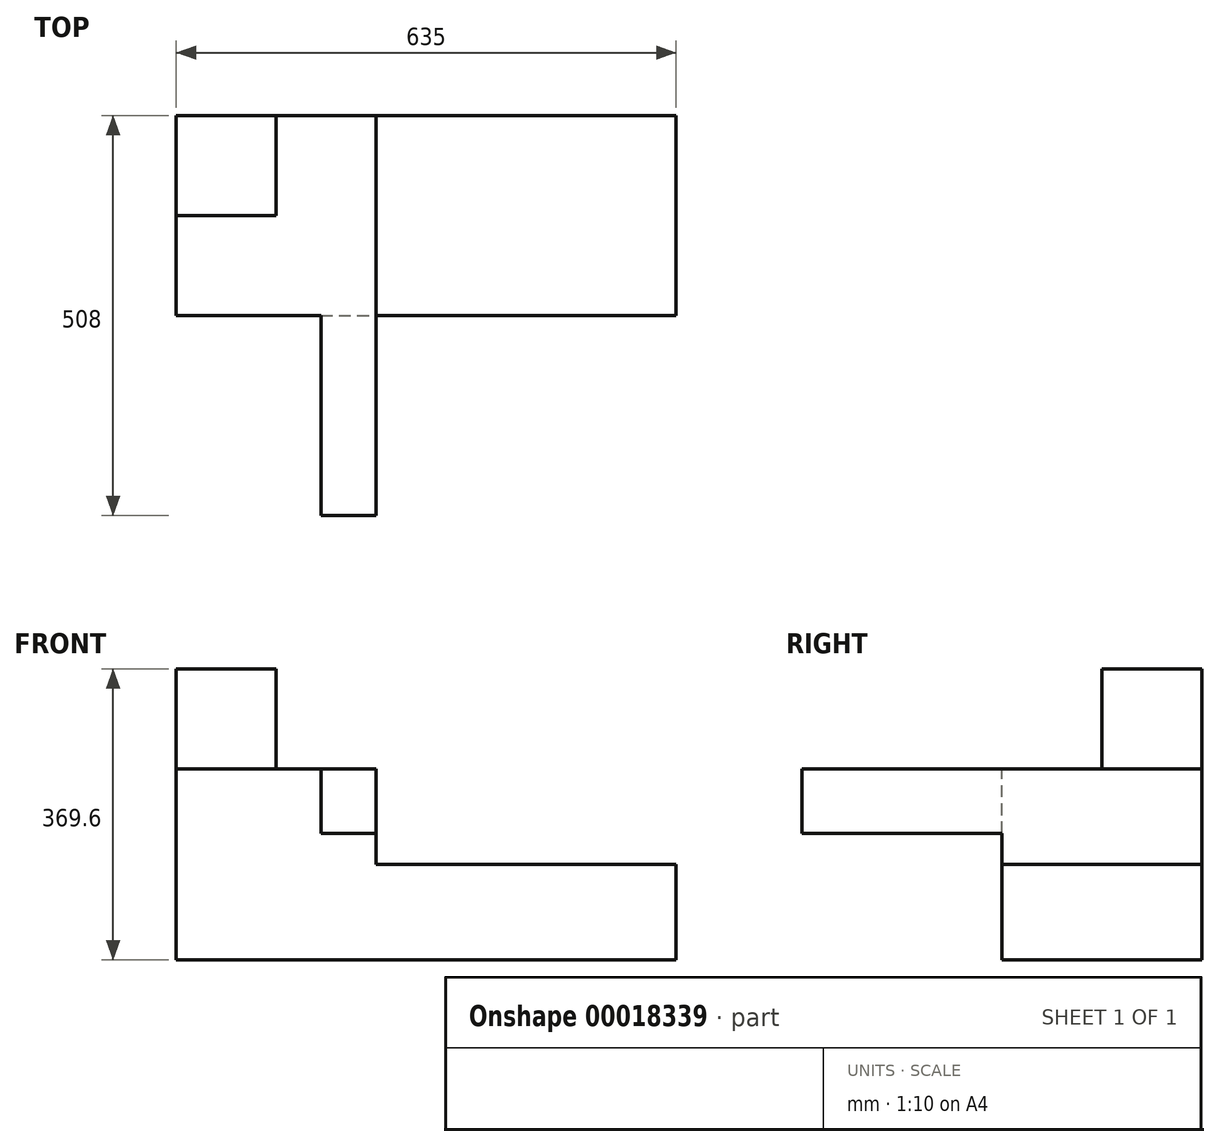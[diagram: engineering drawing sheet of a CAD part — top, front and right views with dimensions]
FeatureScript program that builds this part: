
annotation { "Feature Type Name" : "Feature", "Feature Type Description" : "" }
export const myFeature = defineFeature(function(context is Context, id is Id, definition is map)
    precondition{}
    {
        {
            var Q0;
            Q0=qCreatedBy(makeId("Front.planeOp"),FACE);
            var sketch = newSketch(context, id + "F0", { "sketchPlane" : qUnion([Q0])});
            skLineSegment(sketch, "E0.rect.bottom", {"start": v(127, 121.3) * mm, "end": v(-127, 121.3) * mm});
            skLineSegment(sketch, "E0.rect.top", {"start": v(127, -121.3) * mm, "end": v(-127, -121.3) * mm});
            skLineSegment(sketch, "E0.rect.left", {"start": v(127, 121.3) * mm, "end": v(127, -121.3) * mm});
            skLineSegment(sketch, "E0.rect.right", {"start": v(-127, 121.3) * mm, "end": v(-127, -121.3) * mm});
            skPoint(sketch, "E0.rect.middle", {"position": v(0, 0) * mm});
            skSolve(sketch);
        }
        {
            var Q0;
            Q0=makeQuery(id+"F0.imprint","IMPRINT",FACE,{"disambiguationData":[TD([[makeQuery(id+"F0.imprint","IMPRINT",EDGE,{"derivedFrom":sQuery(id+"F0.wireOp",EDGE,"E0.rect.bottom")}),1.0]])]});
            extrude(context, id + "F1", {"entities" : qUnion([Q0]), "endBound" : BoundingType.SYMMETRIC, "depth" : 254 * mm});
        }
        {
            var Q0;
            Q0=makeQuery(id+"F1.opExtrude","SWEPT_FACE",FACE,{"disambiguationData":[OSD([sQuery(id+"F0.wireOp",EDGE,"E0.rect.bottom")])]});
            var sketch = newSketch(context, id + "F2", { "sketchPlane" : qUnion([Q0])});
            skLineSegment(sketch, "E1.bottom", {"start": v(-127, 127) * mm, "end": v(0, 127) * mm});
            skLineSegment(sketch, "E1.top", {"start": v(-127, 0) * mm, "end": v(0, 0) * mm});
            skLineSegment(sketch, "E1.left", {"start": v(-127, 127) * mm, "end": v(-127, 0) * mm});
            skLineSegment(sketch, "E1.right", {"start": v(0, 127) * mm, "end": v(0, 0) * mm});
            skSolve(sketch);
        }
        {
            var Q0;
            Q0 = qSketchRegion(id + "F2", true);
            extrude(context, id + "F3", {"entities" : qUnion([Q0]), "operationType" : NewBodyOperationType.ADD, "depth" : 127 * mm});
        }
        {
            var Q0;
            Q0=makeQuery(id+"F1.opExtrude","CAP_FACE",FACE,{"disambiguationData":[OSD([sQuery(id+"F0.wireOp",EDGE,"E0.rect.bottom"),sQuery(id+"F0.wireOp",EDGE,"E0.rect.top"),sQuery(id+"F0.wireOp",EDGE,"E0.rect.left"),sQuery(id+"F0.wireOp",EDGE,"E0.rect.right")])],"isStart":false});
            var sketch = newSketch(context, id + "F6", { "sketchPlane" : qUnion([Q0])});
            skLineSegment(sketch, "E2.bottom", {"start": v(56.76, 39.52) * mm, "end": v(127, 39.52) * mm});
            skLineSegment(sketch, "E2.top", {"start": v(56.76, 121.3) * mm, "end": v(127, 121.3) * mm});
            skLineSegment(sketch, "E2.left", {"start": v(56.76, 39.52) * mm, "end": v(56.76, 121.3) * mm});
            skLineSegment(sketch, "E2.right", {"start": v(127, 39.52) * mm, "end": v(127, 121.3) * mm});
            skSolve(sketch);
        }
        {
            var Q0;
            Q0=makeQuery(id+"F6.imprint","IMPRINT",FACE,{"disambiguationData":[TD([[makeQuery(id+"F6.imprint","IMPRINT",EDGE,{"derivedFrom":sQuery(id+"F6.wireOp",EDGE,"E2.bottom")}),1.0]])]});
            extrude(context, id + "F7", {"entities" : qUnion([Q0]), "operationType" : NewBodyOperationType.ADD, "depth" : 254 * mm});
        }
        {
            var Q0;
            Q0=makeQuery(id+"F7.boolean.opBoolean","MERGE",FACE,{"derivedFrom":[makeQuery(id+"F1.opExtrude","SWEPT_FACE",FACE,{"disambiguationData":[OSD([sQuery(id+"F0.wireOp",EDGE,"E0.rect.left")])]}),makeQuery(id+"F7.opExtrude","SWEPT_FACE",FACE,{"disambiguationData":[OSD([sQuery(id+"F6.wireOp",EDGE,"E2.right")])]})]});
            var sketch = newSketch(context, id + "F4", { "sketchPlane" : qUnion([Q0])});
            skLineSegment(sketch, "E3.bottom", {"start": v(-127, -121.3) * mm, "end": v(127, -121.3) * mm});
            skLineSegment(sketch, "E3.top", {"start": v(-127, 0) * mm, "end": v(127, 0) * mm});
            skLineSegment(sketch, "E3.left", {"start": v(-127, -121.3) * mm, "end": v(-127, 0) * mm});
            skLineSegment(sketch, "E3.right", {"start": v(127, -121.3) * mm, "end": v(127, 0) * mm});
            skSolve(sketch);
        }
        {
            var Q0;
            Q0=makeQuery(id+"F4.imprint","IMPRINT",FACE,{"disambiguationData":[TD([[makeQuery(id+"F4.imprint","IMPRINT",EDGE,{"derivedFrom":sQuery(id+"F4.wireOp",EDGE,"E3.bottom")}),1.0]])]});
            extrude(context, id + "F5", {"entities" : qUnion([Q0]), "operationType" : NewBodyOperationType.ADD, "depth" : 381 * mm});
        }
    });
